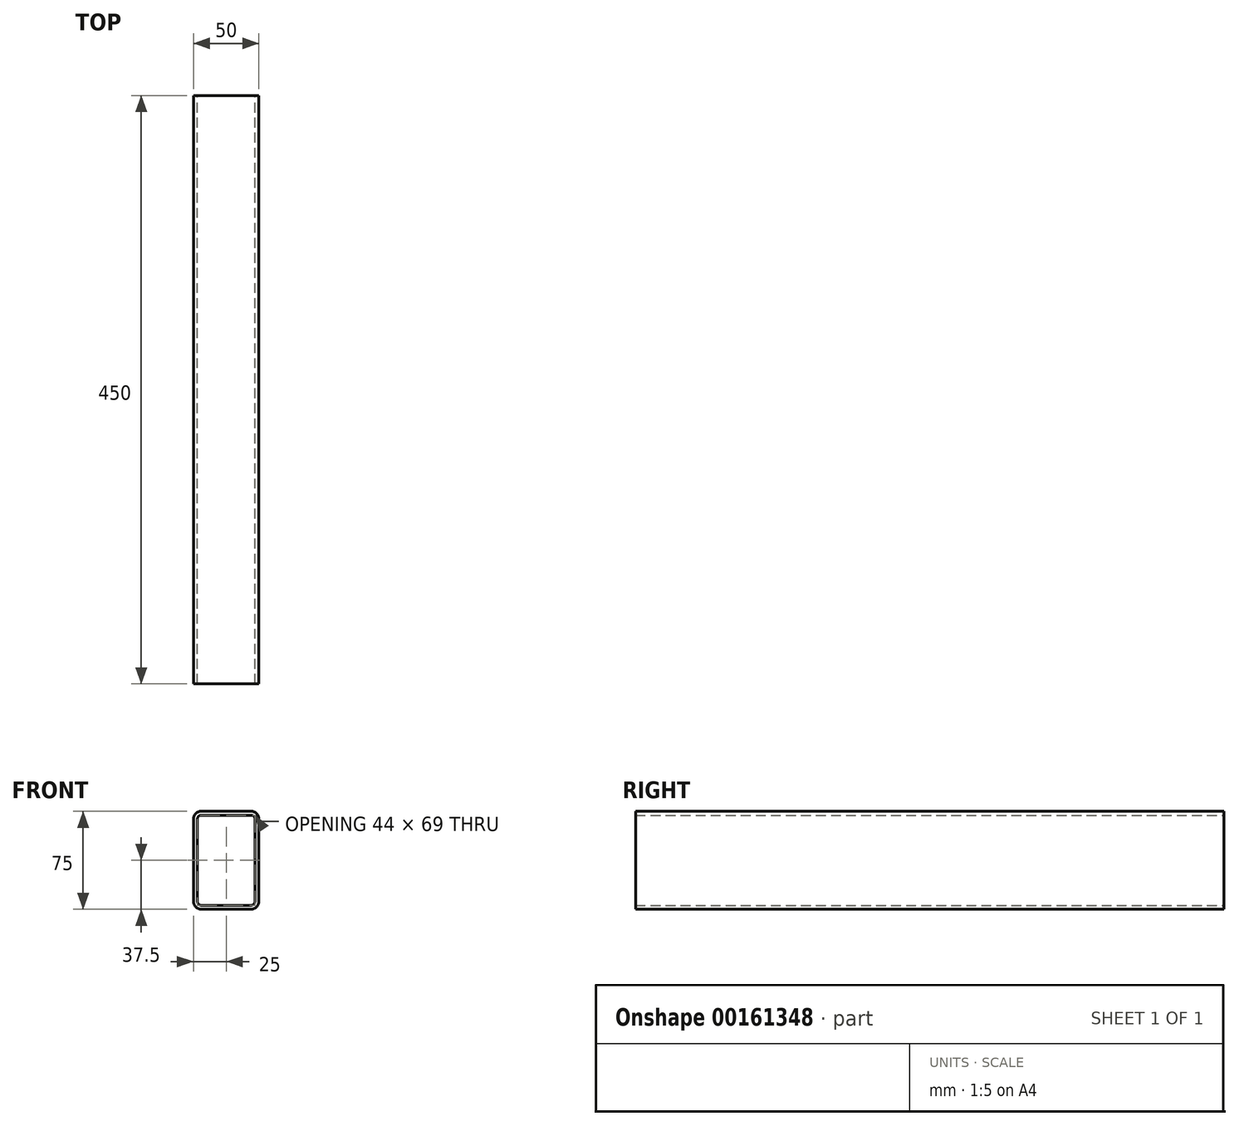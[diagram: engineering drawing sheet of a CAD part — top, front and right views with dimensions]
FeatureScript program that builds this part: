
annotation { "Feature Type Name" : "Feature", "Feature Type Description" : "" }
export const myFeature = defineFeature(function(context is Context, id is Id, definition is map)
    precondition{}
    {
        {
            var Q0;
            Q0=qCreatedBy(makeId("Front.planeOp"),FACE);
            var sketch = newSketch(context, id + "F0", { "sketchPlane" : qUnion([Q0])});
            skLineSegment(sketch, "E0.bottom", {"start": v(25, -37.5) * mm, "end": v(-25, -37.5) * mm});
            skLineSegment(sketch, "E0.top", {"start": v(25, 37.5) * mm, "end": v(-25, 37.5) * mm});
            skLineSegment(sketch, "E0.left", {"start": v(25, -37.5) * mm, "end": v(25, 37.5) * mm});
            skLineSegment(sketch, "E0.right", {"start": v(-25, -37.5) * mm, "end": v(-25, 37.5) * mm});
            skPoint(sketch, "E0.middle", {"position": v(0, 0) * mm});
            skSolve(sketch);
        }
        {
            var Q0;
            Q0 = qSketchRegion(id + "F0", true);
            extrude(context, id + "F1", {"entities" : qUnion([Q0]), "flatOperationType" : FlatOperationType.REMOVE, "offsetDistance" : 25 * mm, "depth" : 450 * mm, "domain" : OperationDomain.MODEL});
        }
        {
            var Q0;
            Q0=makeQuery(id+"F1.opExtrude","SWEPT_EDGE",EDGE,{"disambiguationData":[OSD([sQuery(id+"F0.wireOp",EDGE,"E0.top"),sQuery(id+"F0.wireOp",EDGE,"E0.left")])]});
            var Q1;
            Q1=makeQuery(id+"F1.opExtrude","SWEPT_EDGE",EDGE,{"disambiguationData":[OSD([sQuery(id+"F0.wireOp",EDGE,"E0.top"),sQuery(id+"F0.wireOp",EDGE,"E0.right")])]});
            var Q2;
            Q2=makeQuery(id+"F1.opExtrude","SWEPT_EDGE",EDGE,{"disambiguationData":[OSD([sQuery(id+"F0.wireOp",EDGE,"E0.bottom"),sQuery(id+"F0.wireOp",EDGE,"E0.left")])]});
            var Q3;
            Q3=makeQuery(id+"F1.opExtrude","SWEPT_EDGE",EDGE,{"disambiguationData":[OSD([sQuery(id+"F0.wireOp",EDGE,"E0.bottom"),sQuery(id+"F0.wireOp",EDGE,"E0.right")])]});
            fillet(context, id + "F2", {"entities" : qUnion([Q0, Q1, Q2, Q3]), "radius" : 6 * mm, "tangentPropagation" : true, "allowEdgeOverflow" : false});
        }
        {
            var Q0;
            Q0=makeQuery(id+"F1.opExtrude","CAP_FACE",FACE,{"disambiguationData":[OSD([sQuery(id+"F0.wireOp",EDGE,"E0.bottom"),sQuery(id+"F0.wireOp",EDGE,"E0.top"),sQuery(id+"F0.wireOp",EDGE,"E0.left"),sQuery(id+"F0.wireOp",EDGE,"E0.right")])],"isStart":true});
            var Q1;
            Q1=makeQuery(id+"F1.opExtrude","CAP_FACE",FACE,{"disambiguationData":[OSD([sQuery(id+"F0.wireOp",EDGE,"E0.bottom"),sQuery(id+"F0.wireOp",EDGE,"E0.top"),sQuery(id+"F0.wireOp",EDGE,"E0.left"),sQuery(id+"F0.wireOp",EDGE,"E0.right")])],"isStart":false});
            shell(context, id + "F3", {"entities" : qUnion([Q0, Q1]), "thickness" : 3 * mm});
        }
    });
